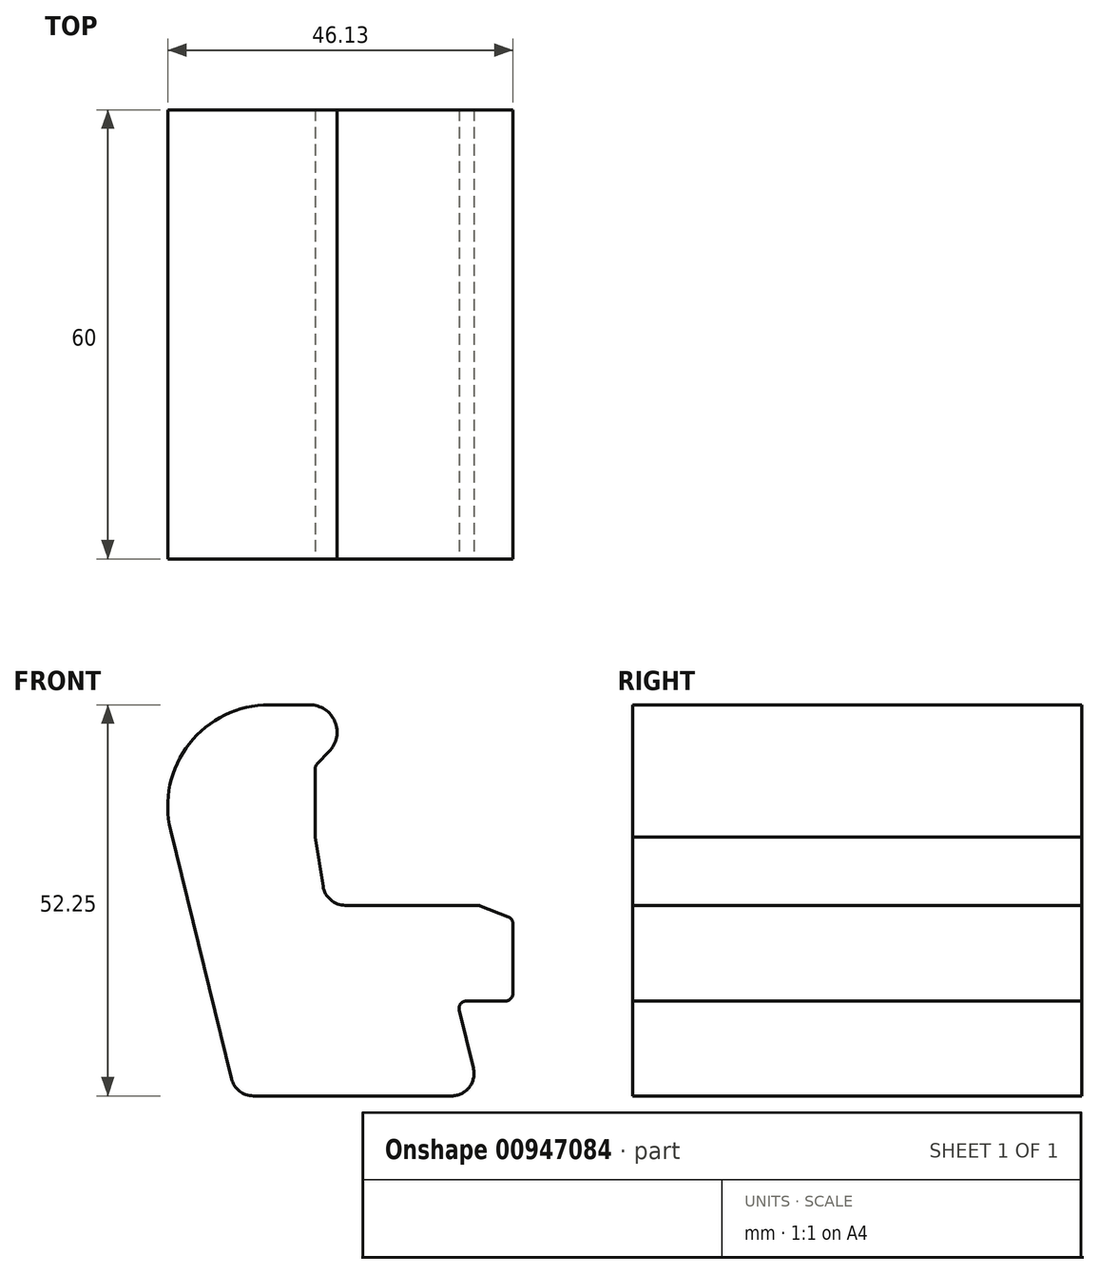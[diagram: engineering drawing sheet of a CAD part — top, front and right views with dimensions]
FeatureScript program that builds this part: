
annotation { "Feature Type Name" : "Feature", "Feature Type Description" : "" }
export const myFeature = defineFeature(function(context is Context, id is Id, definition is map)
    precondition{}
    {
        {
            var Q0;
            Q0=qCreatedBy(makeId("Front.planeOp"),FACE);
            var sketch = newSketch(context, id + "F0", { "sketchPlane" : qUnion([Q0])});
            skLineSegment(sketch, "E0", {"start": v(-35.99, 40.58) * mm, "end": v(-27.85, 7.4) * mm});
            skLineSegment(sketch, "E1", {"start": v(-24.93, 5.12) * mm, "end": v(1.55, 5.12) * mm});
            skLineSegment(sketch, "E2", {"start": v(4.47, 8.83) * mm, "end": v(2.57, 16.56) * mm});
            skLineSegment(sketch, "E3", {"start": v(3.54, 17.8) * mm, "end": v(8.75, 17.8) * mm});
            skLineSegment(sketch, "E4", {"start": v(9.75, 18.8) * mm, "end": v(9.75, 28.13) * mm});
            skLineSegment(sketch, "E5", {"start": v(9.11, 29.06) * mm, "end": v(5.37, 30.52) * mm});
            skLineSegment(sketch, "E6", {"start": v(5, 30.58) * mm, "end": v(-12.66, 30.58) * mm});
            skLineSegment(sketch, "E7", {"start": v(-15.62, 33.11) * mm, "end": v(-16.66, 39.7) * mm});
            skLineSegment(sketch, "E8", {"start": v(-16.66, 39.7) * mm, "end": v(-16.66, 48.84) * mm});
            skArc(sketch, "E9", {"start": v(-22.82, 57.37) * mm, "mid": v(-33.49, 52.18) * mm, "end": v(-35.99, 40.58) * mm});
            skLineSegment(sketch, "E10", {"start": v(-22.82, 57.37) * mm, "end": v(-17.41, 57.37) * mm});
            skArc(sketch, "E11", {"start": v(-17.41, 57.37) * mm, "mid": v(-14.04, 55.13) * mm, "end": v(-14.8, 51.15) * mm});
            skLineSegment(sketch, "E12", {"start": v(-14.8, 51.15) * mm, "end": v(-16.38, 49.53) * mm});
            skPoint(sketch, "E13.visualSharp", {"position": v(-27.29, 5.12) * mm});
            skArc(sketch, "E13.filletArc", {"start": v(-27.85, 7.4) * mm, "mid": v(-26.79, 5.76) * mm, "end": v(-24.93, 5.12) * mm});
            skPoint(sketch, "E14.visualSharp", {"position": v(-15.22, 30.58) * mm});
            skArc(sketch, "E14.filletArc", {"start": v(-15.62, 33.11) * mm, "mid": v(-14.6, 31.3) * mm, "end": v(-12.66, 30.58) * mm});
            skPoint(sketch, "E15.visualSharp", {"position": v(5.38, 5.12) * mm});
            skArc(sketch, "E15.filletArc", {"start": v(1.55, 5.12) * mm, "mid": v(3.91, 6.27) * mm, "end": v(4.47, 8.83) * mm});
            skPoint(sketch, "E16.visualSharp", {"position": v(2.27, 17.8) * mm});
            skArc(sketch, "E16.filletArc", {"start": v(3.54, 17.8) * mm, "mid": v(2.76, 17.42) * mm, "end": v(2.57, 16.56) * mm});
            skPoint(sketch, "E17.visualSharp", {"position": v(9.75, 17.8) * mm});
            skArc(sketch, "E17.filletArc", {"start": v(8.75, 17.8) * mm, "mid": v(9.46, 18.1) * mm, "end": v(9.75, 18.8) * mm});
            skPoint(sketch, "E18.visualSharp", {"position": v(9.75, 28.81) * mm});
            skArc(sketch, "E18.filletArc", {"start": v(9.75, 28.13) * mm, "mid": v(9.58, 28.7) * mm, "end": v(9.11, 29.06) * mm});
            skPoint(sketch, "E19.visualSharp", {"position": v(5.2, 30.58) * mm});
            skArc(sketch, "E19.filletArc", {"start": v(5.37, 30.52) * mm, "mid": v(5.2, 30.57) * mm, "end": v(5, 30.58) * mm});
            skPoint(sketch, "E20.visualSharp", {"position": v(-16.66, 49.24) * mm});
            skArc(sketch, "E20.filletArc", {"start": v(-16.38, 49.53) * mm, "mid": v(-16.59, 49.21) * mm, "end": v(-16.66, 48.84) * mm});
            skSolve(sketch);
        }
        {
            var Q0;
            Q0=makeQuery(id+"F0.imprint","IMPRINT",FACE,{"disambiguationData":[TD([[makeQuery(id+"F0.imprint","IMPRINT",EDGE,{"derivedFrom":sQuery(id+"F0.wireOp",EDGE,"E0")}),1.0]])]});
            extrude(context, id + "F1", {"entities" : qUnion([Q0]), "oppositeDirection" : true, "depth" : 60 * mm, "offsetDistance" : 25 * mm});
        }
    });
